# Revit family: Haworth_JiveTable_HalfRacetrackBases
name_source: partatom
category: Furniture Systems
revit_build: Autodesk Revit 2018 (Build: 20170223_1515(x64)
units: mm (PartAtom-declared; Revit-internal decimal feet)

## family parameters
Always vertical = Yes
Cut with Voids When Loaded = No
OmniClass Number = 23.40.70.14.64.21
OmniClass Title = Systems Furniture
Part Type = Normal
Room Calculation Point = No
Round Connector Dimension = Use Diameter
Shared = No
Work Plane-Based = No

## types (8) — shared parameters
Actual Height = 29"
Assembly Code = E2020200
Custom Size = No
Leg Height = 27 13/16"
Manufacturer = Haworth, Inc.
Max. Depth = 60"
Max. Width = 60"
Min. Depth = 36"
Min. Width = 42"
Model = Haworth Jive
Revision Number = 0
Size = Verify Final Dim. w/ Haworth
Standard Depths = 36, 48, 54, 60 in.
Standard Heights = 29 in.
Standard Widths = 42, 48, 54, 60 in.
Table Thickness = 1 3/16"
URL = http://www.haworth.com
URL - Product = http://www.haworth.com
Warranty = http://www.haworth.com

## per-type parameters (varying)
| type | 2 Column | 4 6 8 Column | 4 Column | 4 Column Support Distance | Actual Depth | Actual Width | Bridge Distance | Casters | Columns | Depth | Description | Glides | Leg Center | Support Distance | Table Radius | Width | X Base 2 3 Column |
| 60d 60w 29h - Bridge Base - With Glides | No | Yes | Yes | 16" | 60" | 60" | 13" | No | No | 60" | Haworth Jive Half Racetrack Bases - 60d 60w 29h - 4 Column - With Glides | Yes | 26" | 15" | 30" | 60" | No |
| 54d 54w 29h - Bridge Base - With Glides | No | Yes | Yes | 11" | 54" | 54" | 13" | No | No | 54" | Haworth Jive Half Racetrack Bases - 54d 54w 29h - 4 Column - With Glides | Yes | 24" | 15" | 27" | 54" | No |
| 48d 48w 29h - Bridge Base - With Glides | Yes | No | No | 11" | 48" | 48" | 13" | No | Yes | 48" | Haworth Jive Half Racetrack Bases - 48d 48w 29h - 2 Column - With Glides | Yes | 22" | 15" | 24" | 48" | Yes |
| 36d 42w 29h - Bridge Base - With Glides | Yes | No | No | 11" | 36" | 42" | 12" | No | Yes | 36" | Haworth Jive Half Racetrack Bases - 36d 42w 29h - 2 Column - With Glides | Yes | 18 3/4" | 14" | 18" | 42" | Yes |
| 36d 42w 29h - Bridge Base - With Casters | Yes | No | No | 11" | 36" | 42" | 12" | Yes | Yes | 36" | Haworth Jive Half Racetrack Bases - 36d 42w 29h - 2 Column - With Glides | No | 18 3/4" | 14" | 18" | 42" | Yes |
| 48d 48w 29h - Bridge Base - With Casters | Yes | No | No | 11" | 48" | 48" | 13" | Yes | Yes | 48" | Haworth Jive Half Racetrack Bases - 48d 48w 29h - 2 Column - With Glides | No | 22" | 15" | 24" | 48" | Yes |
| 54d 54w 29h - Bridge Base - With Casters | No | Yes | Yes | 11" | 54" | 54" | 13" | Yes | No | 54" | Haworth Jive Half Racetrack Bases - 54d 54w 29h - 4 Column - With Casters | No | 24" | 15" | 27" | 54" | No |
| 60d 60w 29h - Bridge Base - With Casters | No | Yes | Yes | 16" | 60" | 60" | 13" | Yes | No | 60" | Haworth Jive Half Racetrack Bases - 60d 60w 29h - 4 Column - With Casters | No | 26" | 15" | 30" | 60" | No |

## geometry (parser evidence)
native form markers: Sweep x21
no freeform markers — native parametric forms only
